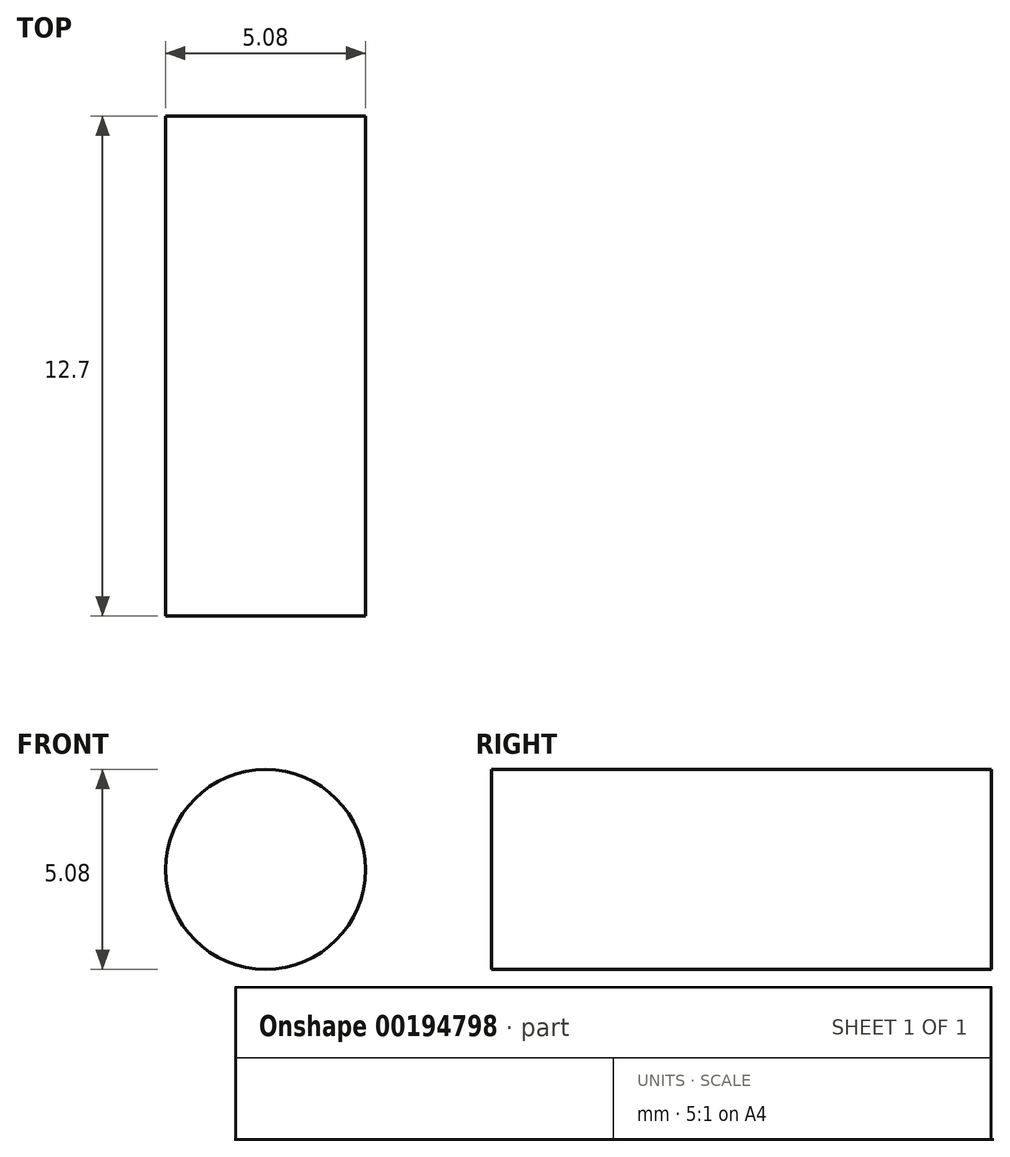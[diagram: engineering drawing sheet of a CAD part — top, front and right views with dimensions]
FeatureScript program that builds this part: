
annotation { "Feature Type Name" : "Feature", "Feature Type Description" : "" }
export const myFeature = defineFeature(function(context is Context, id is Id, definition is map)
    precondition{}
    {
        {
            var Q0;
            Q0=qCreatedBy(makeId("Front.planeOp"),FACE);
            var sketch = newSketch(context, id + "F0", { "sketchPlane" : qUnion([Q0])});
            skCircle(sketch, "E0", {"center": v(0, 0) * mm, "radius": 2.54 * mm});
            skSolve(sketch);
        }
        {
            var Q0;
            Q0=makeQuery(id+"F0.imprint","IMPRINT",FACE,{"disambiguationData":[TD([[makeQuery(id+"F0.imprint","IMPRINT",EDGE,{"derivedFrom":sQuery(id+"F0.wireOp",EDGE,"E0")}),1.0]])]});
            extrude(context, id + "F1", {"entities" : qUnion([Q0]), "depth" : 12.7 * mm});
        }
        {
            var Q0;
            Q0=makeQuery(id+"F0.imprint","IMPRINT",FACE,{"disambiguationData":[TD([[makeQuery(id+"F0.imprint","IMPRINT",EDGE,{"derivedFrom":sQuery(id+"F0.wireOp",EDGE,"E0")}),1.0]])]});
            extrude(context, id + "F2", {"entities" : qUnion([Q0]), "depth" : 12.7 * mm});
        }
    });
